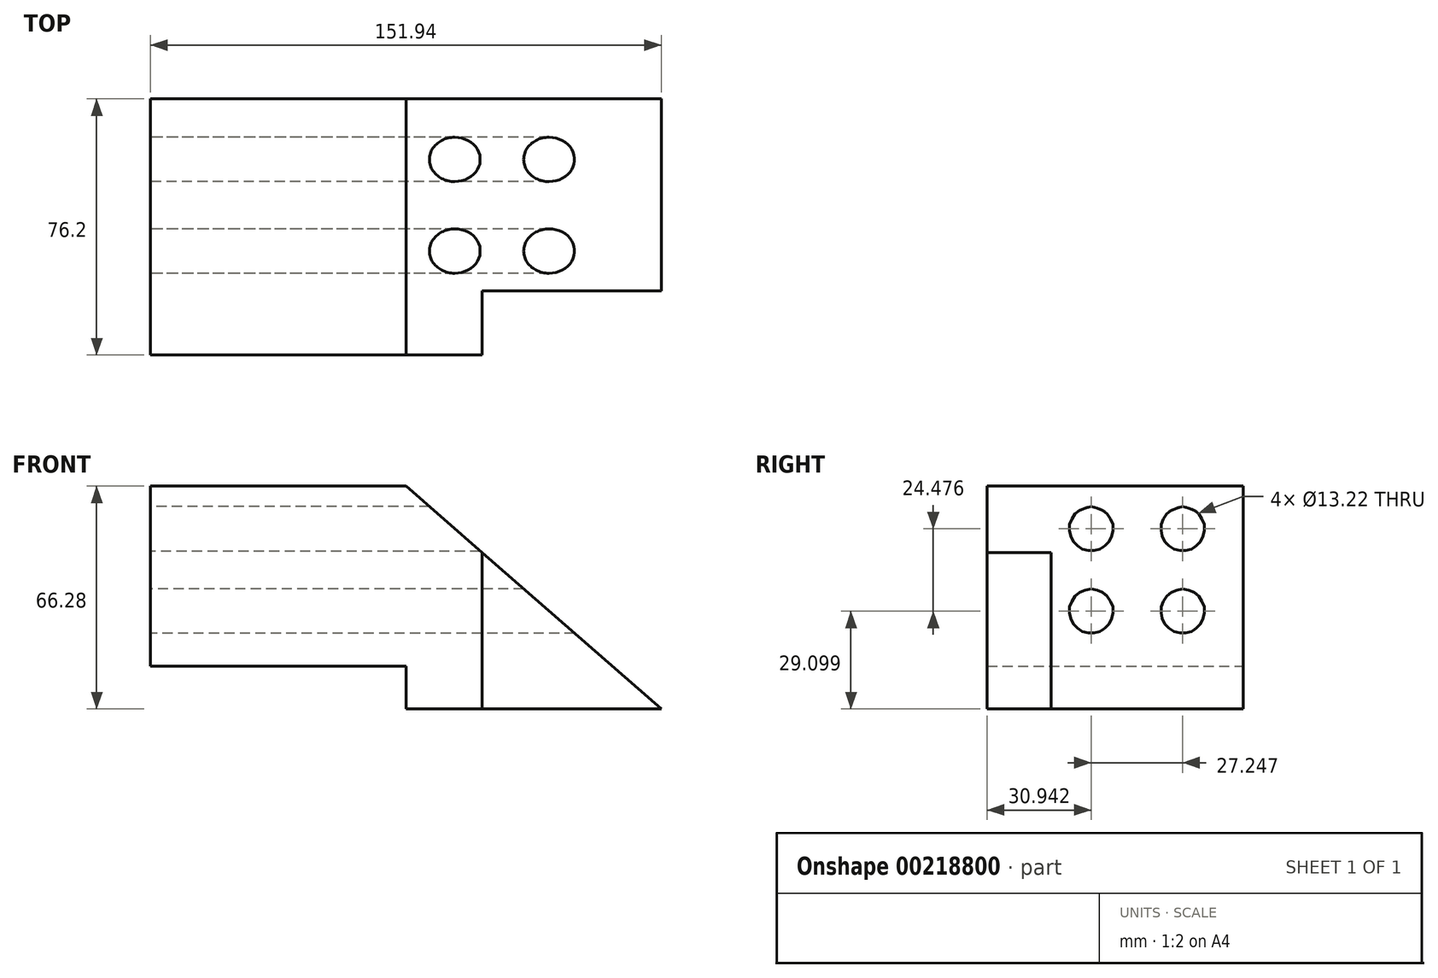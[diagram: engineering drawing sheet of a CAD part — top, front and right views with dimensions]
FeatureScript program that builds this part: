
annotation { "Feature Type Name" : "Feature", "Feature Type Description" : "" }
export const myFeature = defineFeature(function(context is Context, id is Id, definition is map)
    precondition{}
    {
        {
            var Q0;
            Q0=qCreatedBy(makeId("Front.planeOp"),FACE);
            var sketch = newSketch(context, id + "F0", { "sketchPlane" : qUnion([Q0])});
            skLineSegment(sketch, "E0.bottom", {"start": v(75.97, -33.14) * mm, "end": v(0, -33.14) * mm});
            skLineSegment(sketch, "E0.top", {"start": v(0, 33.14) * mm, "end": v(-75.97, 33.14) * mm});
            skLineSegment(sketch, "E0.right", {"start": v(-75.97, -20.44) * mm, "end": v(-75.97, 33.14) * mm});
            skPoint(sketch, "E0.middle", {"position": v(0, 0) * mm});
            skLineSegment(sketch, "E1.bottom", {"start": v(-75.97, -20.44) * mm, "end": v(0, -20.44) * mm});
            skLineSegment(sketch, "E1.right", {"start": v(0, -20.44) * mm, "end": v(0, -33.14) * mm});
            skPoint(sketch, "E2.orphan", {"position": v(-75.97, -33.14) * mm});
            skLineSegment(sketch, "E3", {"start": v(0, 33.14) * mm, "end": v(75.97, -33.14) * mm});
            skPoint(sketch, "E0.left.end.orphan", {"position": v(75.97, 33.14) * mm});
            skSolve(sketch);
        }
        {
            var Q0;
            Q0=makeQuery(id+"F0.imprint","IMPRINT",FACE,{"disambiguationData":[TD([[makeQuery(id+"F0.imprint","IMPRINT",EDGE,{"derivedFrom":sQuery(id+"F0.wireOp",EDGE,"E0.bottom")}),-1.0]])]});
            extrude(context, id + "F1", {"entities" : qUnion([Q0]), "endBound" : BoundingType.SYMMETRIC, "depth" : 76.2 * mm});
        }
        {
            var Q0;
            Q0=makeQuery(id+"F1.opExtrude","CAP_FACE",FACE,{"disambiguationData":[OSD([sQuery(id+"F0.wireOp",EDGE,"E0.bottom"),sQuery(id+"F0.wireOp",EDGE,"E0.top"),sQuery(id+"F0.wireOp",EDGE,"E0.right"),sQuery(id+"F0.wireOp",EDGE,"E1.bottom"),sQuery(id+"F0.wireOp",EDGE,"E1.right"),sQuery(id+"F0.wireOp",EDGE,"E3")])],"isStart":false});
            var sketch = newSketch(context, id + "F2", { "sketchPlane" : qUnion([Q0])});
            skLineSegment(sketch, "E4.bottom", {"start": v(75.97, -33.14) * mm, "end": v(22.7, -33.14) * mm});
            skLineSegment(sketch, "E4.right", {"start": v(22.7, -33.14) * mm, "end": v(22.7, 13.33) * mm});
            skLineSegment(sketch, "E5", {"start": v(22.7, 13.33) * mm, "end": v(75.97, -33.14) * mm});
            skSolve(sketch);
        }
        {
            var Q0;
            Q0=makeQuery(id+"F2.imprint","IMPRINT",FACE,{"disambiguationData":[TD([[makeQuery(id+"F2.imprint","IMPRINT",EDGE,{"derivedFrom":sQuery(id+"F2.wireOp",EDGE,"E4.bottom")}),-1.0]])]});
            extrude(context, id + "F3", {"entities" : qUnion([Q0]), "operationType" : NewBodyOperationType.REMOVE, "oppositeDirection" : true, "depth" : 19.05 * mm});
        }
        {
            var Q0;
            Q0=makeQuery(id+"F1.opExtrude","SWEPT_FACE",FACE,{"disambiguationData":[OSD([sQuery(id+"F0.wireOp",EDGE,"E0.right")])]});
            var sketch = newSketch(context, id + "F4", { "sketchPlane" : qUnion([Q0])});
            skCircle(sketch, "E6", {"center": v(7.16, 20.44) * mm, "radius": 6.61 * mm});
            skCircle(sketch, "E7", {"center": v(-20.09, 20.44) * mm, "radius": 6.61 * mm});
            skCircle(sketch, "E8", {"center": v(-20.09, -4.04) * mm, "radius": 6.61 * mm});
            skCircle(sketch, "E9", {"center": v(7.16, -4.04) * mm, "radius": 6.61 * mm});
            skSolve(sketch);
        }
        {
            var Q0;
            Q0=makeQuery(id+"F4.imprint","IMPRINT",FACE,{"disambiguationData":[TD([[makeQuery(id+"F4.imprint","IMPRINT",EDGE,{"derivedFrom":sQuery(id+"F4.wireOp",EDGE,"E6")}),1.0]])]});
            var Q1;
            Q1=makeQuery(id+"F4.imprint","IMPRINT",FACE,{"disambiguationData":[TD([[makeQuery(id+"F4.imprint","IMPRINT",EDGE,{"derivedFrom":sQuery(id+"F4.wireOp",EDGE,"E8")}),1.0]])]});
            var Q2;
            Q2=makeQuery(id+"F4.imprint","IMPRINT",FACE,{"disambiguationData":[TD([[makeQuery(id+"F4.imprint","IMPRINT",EDGE,{"derivedFrom":sQuery(id+"F4.wireOp",EDGE,"E9")}),1.0]])]});
            var Q3;
            Q3=makeQuery(id+"F4.imprint","IMPRINT",FACE,{"disambiguationData":[TD([[makeQuery(id+"F4.imprint","IMPRINT",EDGE,{"derivedFrom":sQuery(id+"F4.wireOp",EDGE,"E7")}),1.0]])]});
            extrude(context, id + "F5", {"entities" : qUnion([Q0, Q1, Q2, Q3]), "operationType" : NewBodyOperationType.REMOVE, "oppositeDirection" : true, "depth" : 254 * mm});
        }
    });
